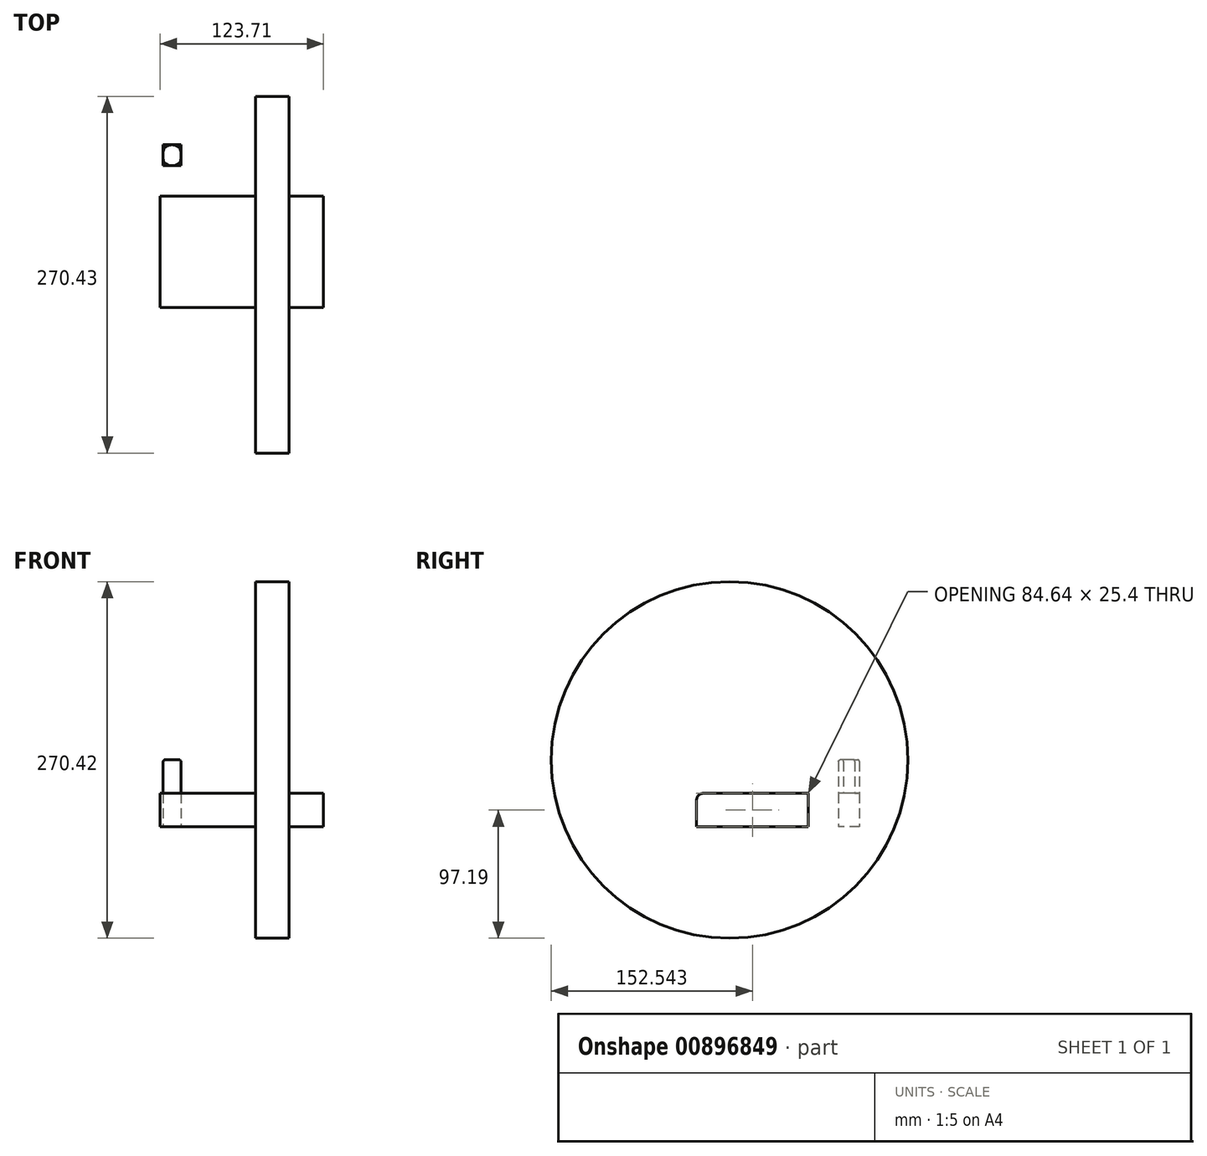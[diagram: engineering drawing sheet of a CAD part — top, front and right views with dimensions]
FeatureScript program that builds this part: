
annotation { "Feature Type Name" : "Feature", "Feature Type Description" : "" }
export const myFeature = defineFeature(function(context is Context, id is Id, definition is map)
    precondition{}
    {
        {
            var Q0;
            Q0=qCreatedBy(makeId("Top.planeOp"),FACE);
            var sketch = newSketch(context, id + "F0", { "sketchPlane" : qUnion([Q0])});
            skLineSegment(sketch, "E0.bottom", {"start": v(-72.39, 29.85) * mm, "end": v(51.32, 29.85) * mm});
            skLineSegment(sketch, "E0.top", {"start": v(-72.39, -54.79) * mm, "end": v(51.32, -54.79) * mm});
            skLineSegment(sketch, "E0.left", {"start": v(-72.39, 29.85) * mm, "end": v(-72.39, -54.79) * mm});
            skLineSegment(sketch, "E0.right", {"start": v(51.32, 29.85) * mm, "end": v(51.32, -54.79) * mm});
            skSolve(sketch);
        }
        {
            var Q0;
            Q0=makeQuery(id+"F0.imprint","IMPRINT",FACE,{"disambiguationData":[TD([[makeQuery(id+"F0.imprint","IMPRINT",EDGE,{"derivedFrom":sQuery(id+"F0.wireOp",EDGE,"E0.bottom")}),-1.0]])]});
            extrude(context, id + "F1", {"entities" : qUnion([Q0]), "depth" : 25.4 * mm, "offsetDistance" : 25.4 * mm});
        }
        {
            var Q0;
            Q0=makeQuery(id+"F1.opExtrude","CAP_EDGE",EDGE,{"disambiguationData":[OSD([sQuery(id+"F0.wireOp",EDGE,"E0.top")])],"isStart":false});
            fillet(context, id + "F2", {"entities" : qUnion([Q0]), "radius" : 5.08 * mm, "tangentPropagation" : true, "allowEdgeOverflow" : false});
        }
        {
            var Q0;
            Q0=qCreatedBy(makeId("Right.planeOp"),FACE);
            var sketch = newSketch(context, id + "F3", { "sketchPlane" : qUnion([Q0])});
            skCircle(sketch, "E1", {"center": v(-29.8, 50.72) * mm, "radius": 135.21 * mm});
            skSolve(sketch);
        }
        {
            var Q0;
            Q0=makeQuery(id+"F3.imprint","IMPRINT",FACE,{"disambiguationData":[TD([[makeQuery(id+"F3.imprint","IMPRINT",EDGE,{"derivedFrom":sQuery(id+"F3.wireOp",EDGE,"E1")}),1.0]])]});
            extrude(context, id + "F4", {"entities" : qUnion([Q0]), "operationType" : NewBodyOperationType.ADD, "depth" : 25.4 * mm, "offsetDistance" : 25.4 * mm});
        }
        {
            var Q0;
            Q0=qCreatedBy(makeId("Top.planeOp"),FACE);
            var sketch = newSketch(context, id + "F5", { "sketchPlane" : qUnion([Q0])});
            skLineSegment(sketch, "E2.bottom", {"start": v(-70.1, 68.7) * mm, "end": v(-56.7, 68.7) * mm});
            skLineSegment(sketch, "E2.top", {"start": v(-70.1, 52.85) * mm, "end": v(-56.7, 52.85) * mm});
            skLineSegment(sketch, "E2.left", {"start": v(-70.1, 68.7) * mm, "end": v(-70.1, 52.85) * mm});
            skLineSegment(sketch, "E2.right", {"start": v(-56.7, 68.7) * mm, "end": v(-56.7, 52.85) * mm});
            skSolve(sketch);
        }
        {
            var Q0;
            Q0=makeQuery(id+"F5.imprint","IMPRINT",FACE,{"disambiguationData":[TD([[makeQuery(id+"F5.imprint","IMPRINT",EDGE,{"derivedFrom":sQuery(id+"F5.wireOp",EDGE,"E2.bottom")}),-1.0]])]});
            extrude(context, id + "F6", {"entities" : qUnion([Q0]), "depth" : 25.4 * mm, "offsetDistance" : 25.4 * mm});
        }
        {
            var Q0;
            Q0=makeQuery(id+"F6.opExtrude","CAP_FACE",FACE,{"disambiguationData":[OSD([sQuery(id+"F5.wireOp",EDGE,"E2.bottom"),sQuery(id+"F5.wireOp",EDGE,"E2.top"),sQuery(id+"F5.wireOp",EDGE,"E2.left"),sQuery(id+"F5.wireOp",EDGE,"E2.right")])],"isStart":false});
            var sketch = newSketch(context, id + "F7", { "sketchPlane" : qUnion([Q0])});
            skCircle(sketch, "E3", {"center": v(-63.4, 60.78) * mm, "radius": 7.93 * mm});
            skPoint(sketch, "E3.centerSnap0", {"position": v(-63.4, 52.85) * mm});
            skPoint(sketch, "E3.centerSnap1", {"position": v(-56.7, 60.78) * mm});
            skSolve(sketch);
        }
        {
            var Q0;
            {var subQ0=sQuery(id+"F7.wireOp",EDGE,"E3");var subQ7=makeQuery(id+"F7.imprint","INTERSECT",VERTEX,{"derivedFrom":[makeQuery(id+"F6.opExtrude","CAP_EDGE",EDGE,{"disambiguationData":[OSD([sQuery(id+"F5.wireOp",EDGE,"E2.bottom")])],"isStart":false}),subQ0]});Q0=makeQuery(id+"F7.imprint","IMPRINT",FACE,{"disambiguationData":[TD([[makeQuery(id+"F7.imprint","IMPRINT",EDGE,{"disambiguationData":[TD([[subQ7,1.0]])],"derivedFrom":subQ0}),1.0]])]});}
            var Q1;
            Q1=sQuery(id+"F7.wireOp",EDGE,"E3");
            extrude(context, id + "F8", {"entities" : qUnion([Q0]), "surfaceEntities" : qUnion([Q1]), "depth" : 25.4 * mm, "offsetDistance" : 25.4 * mm});
        }
        {
            var Q0;
            Q0=makeQuery(id+"F8.opExtrude","CAP_FACE",FACE,{"disambiguationData":[OSD([sQuery(id+"F5.wireOp",EDGE,"E2.left"),sQuery(id+"F5.wireOp",EDGE,"E2.right"),sQuery(id+"F7.wireOp",EDGE,"E3")])],"isStart":false});
            fillet(context, id + "F9", {"entities" : qUnion([Q0]), "radius" : 1.27 * mm, "tangentPropagation" : true, "allowEdgeOverflow" : false});
        }
    });
